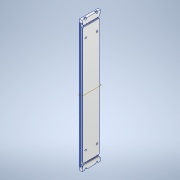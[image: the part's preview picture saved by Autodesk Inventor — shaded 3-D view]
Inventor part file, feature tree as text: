
AUTODESK INVENTOR PART (.ipt)
format: ipt  version: 2020.1 (Build 241239000, 239)  size: 259,584 bytes
history: native  units: mm
features: sketch x4, extrude x3, other x2, chamfer x1, hole x1, mirror x1, fillet x1
ambient origin geometry x8: Origin, YZ Plane, XZ Plane, XY Plane, X Axis, Y Axis, Z Axis, Center Point
bodies: Body1 (feature_tree)
feature tree (13):
  other  "Твердое тело1"
  extrude  "Выдавливание1"  Depth=14.0mm
  extrude  "Выдавливание3"  Depth=6.5mm
  extrude  "Выдавливание4"  Depth=6.5mm
  chamfer  "Фаска2"  Distance=2.5mm
  sketch  "Эскиз7"
  other  "РабПлоскость1"
  hole  "Отверстие1"  [1 undecoded]
  mirror  "Зеркальное отражение1"
  fillet  "Сопряжение2"  Radius=2.0mm
  sketch  "Эскиз1"
  sketch  "Эскиз5"
  sketch  "Эскиз6"
note: 1 required parameter value undecoded (feature->parameter linkage not recoverable at this tier; creation-order binding heuristic only, values carry confidence <= 0.55)
